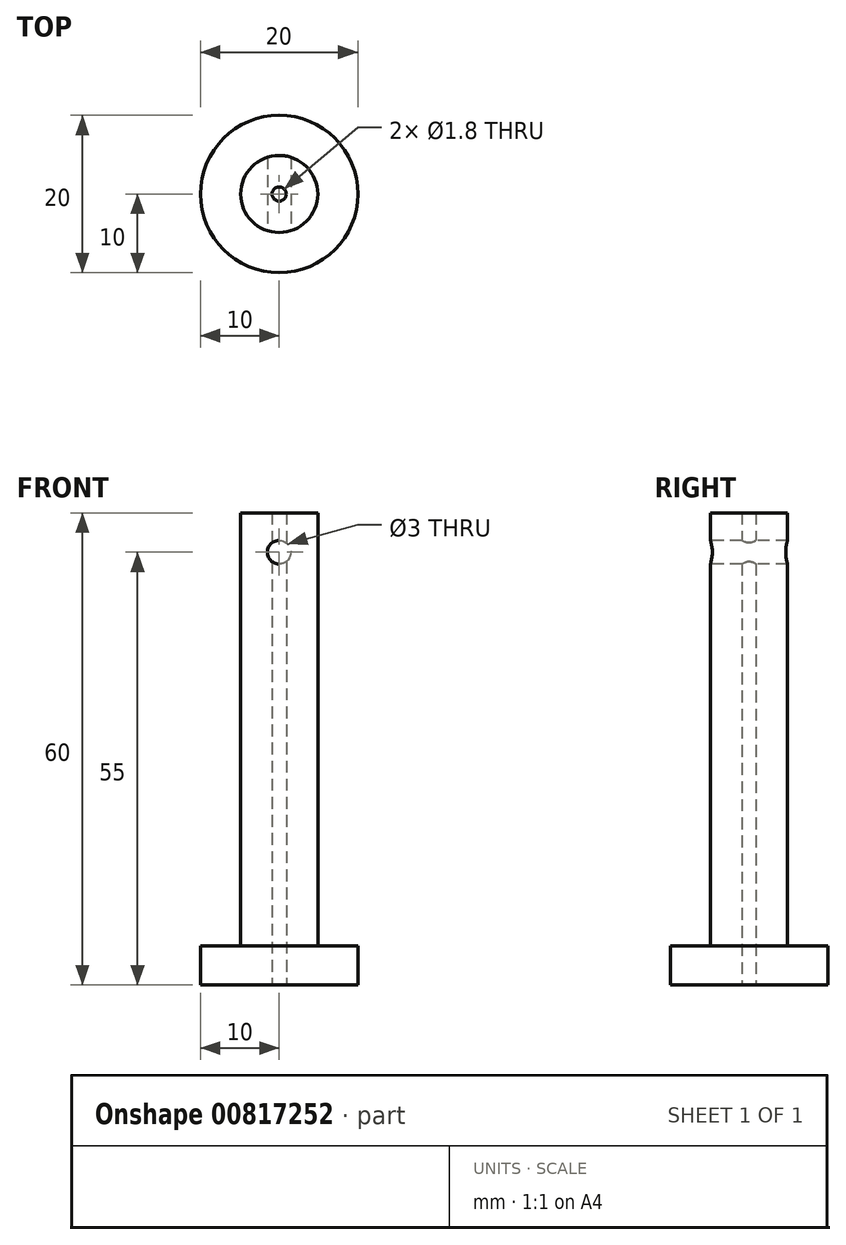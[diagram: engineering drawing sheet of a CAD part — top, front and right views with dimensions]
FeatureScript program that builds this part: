
annotation { "Feature Type Name" : "Feature", "Feature Type Description" : "" }
export const myFeature = defineFeature(function(context is Context, id is Id, definition is map)
    precondition{}
    {
        {
            var Q0;
            Q0=qCreatedBy(makeId("Top.planeOp"),FACE);
            var sketch = newSketch(context, id + "F0", { "sketchPlane" : qUnion([Q0])});
            skCircle(sketch, "E0", {"center": v(0, 0) * mm, "radius": 10 * mm});
            skCircle(sketch, "E1", {"center": v(0, 0) * mm, "radius": 4.9 * mm});
            skCircle(sketch, "E2", {"center": v(0, 0) * mm, "radius": 0.9 * mm});
            skSolve(sketch);
        }
        {
            var Q0;
            Q0=makeQuery(id+"F0.imprint","IMPRINT",FACE,{"disambiguationData":[TD([[makeQuery(id+"F0.imprint","IMPRINT",EDGE,{"derivedFrom":sQuery(id+"F0.wireOp",EDGE,"E1")}),1.0]])]});
            extrude(context, id + "F1", {"entities" : qUnion([Q0]), "depth" : 60 * mm, "offsetDistance" : 25 * mm});
        }
        {
            var Q0;
            Q0=makeQuery(id+"F0.imprint","IMPRINT",FACE,{"disambiguationData":[TD([[makeQuery(id+"F0.imprint","IMPRINT",EDGE,{"derivedFrom":sQuery(id+"F0.wireOp",EDGE,"E0")}),1.0]])]});
            extrude(context, id + "F2", {"entities" : qUnion([Q0]), "operationType" : NewBodyOperationType.ADD, "depth" : 5 * mm, "offsetDistance" : 25 * mm});
        }
        {
            var Q0;
            Q0=qCreatedBy(makeId("Front.planeOp"),FACE);
            var sketch = newSketch(context, id + "F3", { "sketchPlane" : qUnion([Q0])});
            skPoint(sketch, "E3", {"position": v(0, 55) * mm});
            skSolve(sketch);
        }
        {
            var Q0;
            Q0=sQuery(id+"F3.wireOp",VERTEX,"E3");
            var Q1;
            Q1=makeQuery(id+"F1.opExtrude","SWEPT_BODY",BODY,{"disambiguationData":[OSD([sQuery(id+"F0.wireOp",EDGE,"E1"),sQuery(id+"F0.wireOp",EDGE,"E2")])]});
            hole(context, id + "F4", {"style" : HoleStyle.SIMPLE, "endStyle" : HoleEndStyle.THROUGH, "holeDiameter" : 3 * mm, "majorDiameter" : 5 * mm, "isTappedThrough" : true, "tappedDepth" : 12 * mm, "tapClearance" : 3, "locations" : qUnion([Q0]), "scope" : qUnion([Q1])});
        }
        {
            var Q0;
            Q0=sQuery(id+"F3.wireOp",VERTEX,"E3");
            var Q1;
            Q1=makeQuery(id+"F1.opExtrude","SWEPT_BODY",BODY,{"disambiguationData":[OSD([sQuery(id+"F0.wireOp",EDGE,"E1"),sQuery(id+"F0.wireOp",EDGE,"E2")])]});
            hole(context, id + "F5", {"style" : HoleStyle.SIMPLE, "endStyle" : HoleEndStyle.THROUGH, "oppositeDirection" : true, "holeDiameter" : 3 * mm, "majorDiameter" : 5 * mm, "isTappedThrough" : true, "tappedDepth" : 12 * mm, "tapClearance" : 3, "locations" : qUnion([Q0]), "scope" : qUnion([Q1])});
        }
    });
